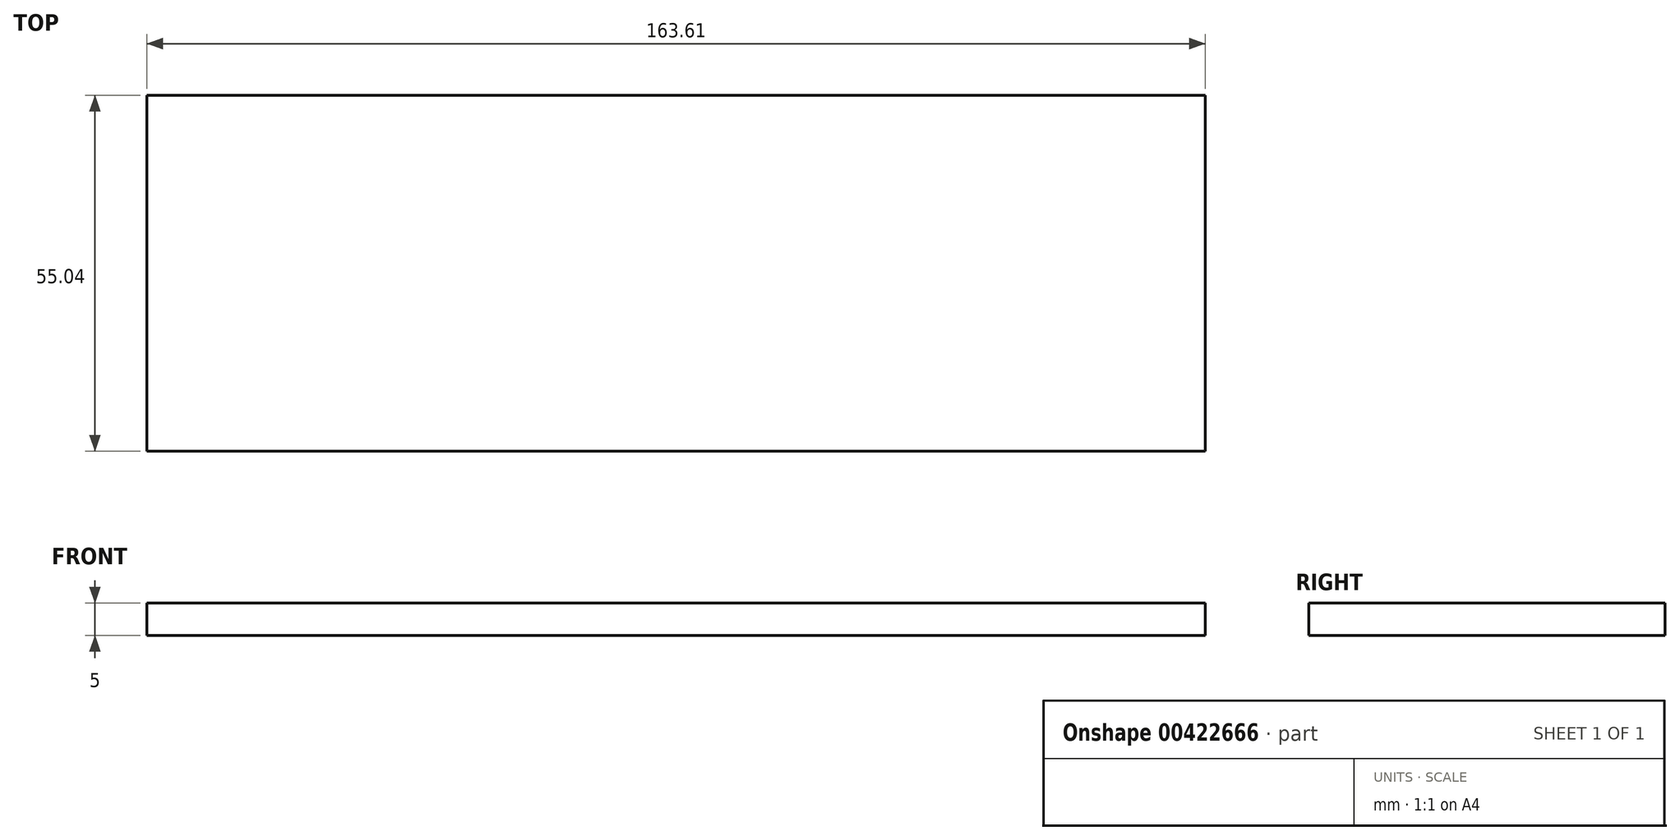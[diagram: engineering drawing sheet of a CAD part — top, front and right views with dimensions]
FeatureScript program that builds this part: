
annotation { "Feature Type Name" : "Feature", "Feature Type Description" : "" }
export const myFeature = defineFeature(function(context is Context, id is Id, definition is map)
    precondition{}
    {
        {
            var Q0;
            Q0=qCreatedBy(makeId("Top.planeOp"),FACE);
            var sketch = newSketch(context, id + "F0", { "sketchPlane" : qUnion([Q0])});
            skLineSegment(sketch, "E0.top", {"start": v(-148.44, -86.68) * mm, "end": v(-7.53, -86.68) * mm});
            skLineSegment(sketch, "E1", {"start": v(-7.53, -86.68) * mm, "end": v(-1.18, -86.68) * mm});
            skLineSegment(sketch, "E2", {"start": v(-148.44, -86.68) * mm, "end": v(-154.8, -86.68) * mm});
            skLineSegment(sketch, "E3", {"start": v(-1.18, -86.68) * mm, "end": v(8.82, -86.68) * mm});
            skLineSegment(sketch, "E4", {"start": v(8.82, -86.68) * mm, "end": v(8.82, -31.64) * mm});
            skLineSegment(sketch, "E5", {"start": v(8.82, -31.64) * mm, "end": v(-154.8, -31.64) * mm});
            skLineSegment(sketch, "E6", {"start": v(-154.8, -31.64) * mm, "end": v(-154.8, -86.68) * mm});
            skSolve(sketch);
        }
        {
            var Q0;
            Q0 = qSketchRegion(id + "F0", true);
            extrude(context, id + "F1", {"entities" : qUnion([Q0]), "depth" : 5 * mm});
        }
    });
